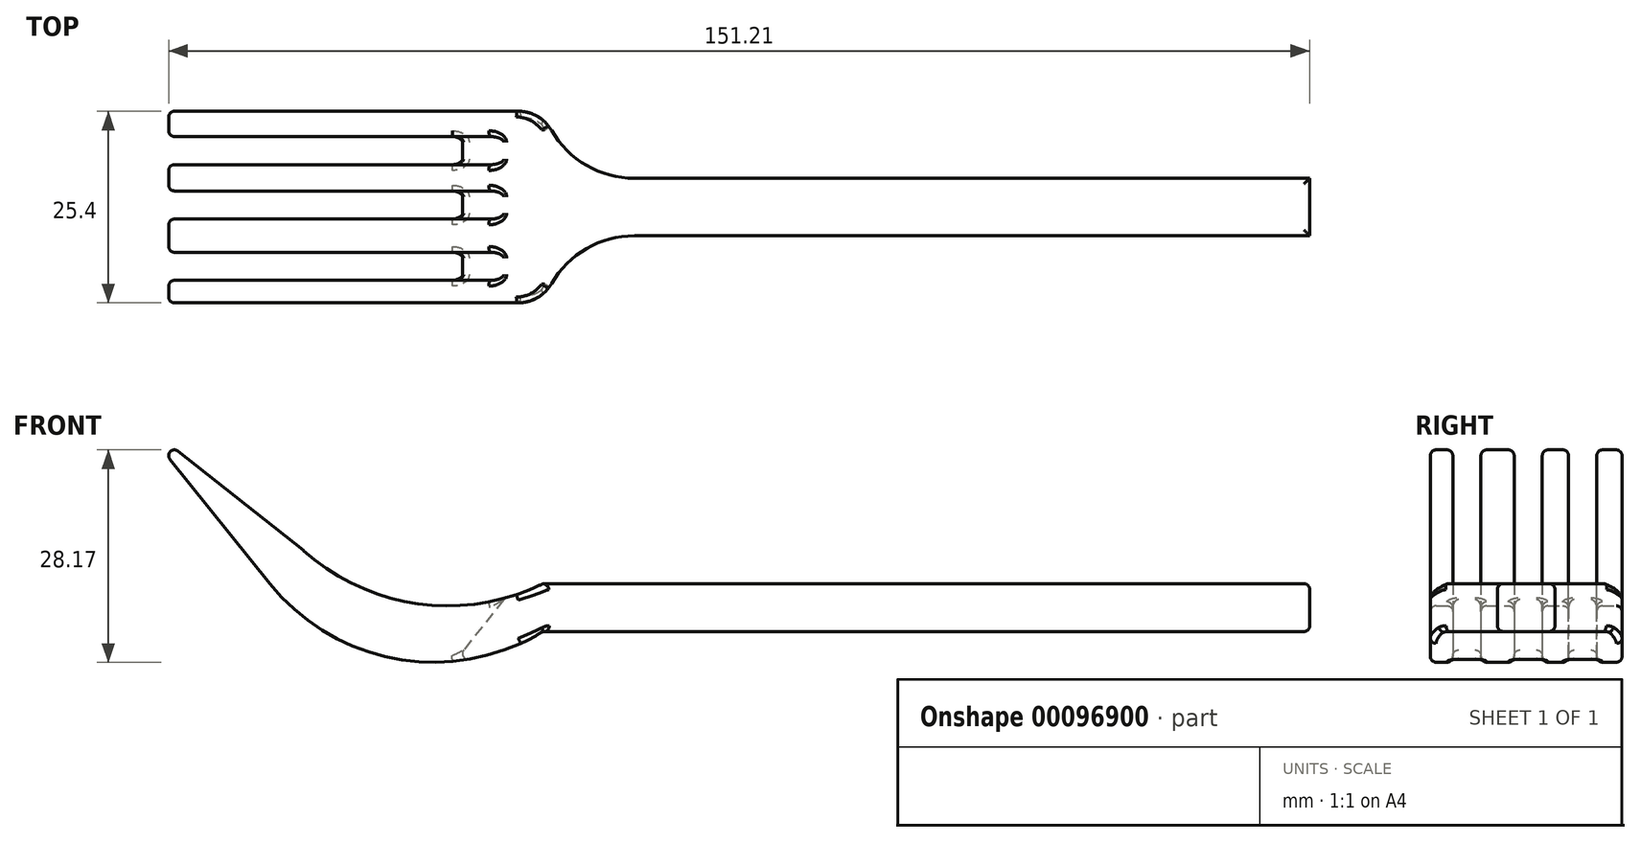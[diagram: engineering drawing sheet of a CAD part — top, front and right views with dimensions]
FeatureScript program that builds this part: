
annotation { "Feature Type Name" : "Feature", "Feature Type Description" : "" }
export const myFeature = defineFeature(function(context is Context, id is Id, definition is map)
    precondition{}
    {
        {
            var Q0;
            Q0=qCreatedBy(makeId("Front.planeOp"),FACE);
            var sketch = newSketch(context, id + "F0", { "sketchPlane" : qUnion([Q0])});
            skLineSegment(sketch, "E0.bottom", {"start": v(-0.74, 15.4) * mm, "end": v(100.86, 15.4) * mm});
            skLineSegment(sketch, "E0.top", {"start": v(-0.74, 9.04) * mm, "end": v(100.86, 9.04) * mm});
            skLineSegment(sketch, "E0.right", {"start": v(100.86, 15.4) * mm, "end": v(100.86, 9.04) * mm});
            skArc(sketch, "E1", {"start": v(-36.94, 15.4) * mm, "mid": v(-20.03, 5.4) * mm, "end": v(-0.74, 9.04) * mm});
            skArc(sketch, "E2", {"start": v(-32.49, 19.8) * mm, "mid": v(-17.29, 12.72) * mm, "end": v(-0.74, 15.4) * mm});
            skPoint(sketch, "E3.start.orphan", {"position": v(-45.23, 31.3) * mm});
            skPoint(sketch, "E4.end.orphan", {"position": v(-49.7, 31.3) * mm});
            skLineSegment(sketch, "E5", {"start": v(-36.94, 15.4) * mm, "end": v(-54.4, 37.16) * mm});
            skLineSegment(sketch, "E6", {"start": v(-54.4, 37.16) * mm, "end": v(-32.49, 19.8) * mm});
            skSolve(sketch);
        }
        {
            var Q0;
            Q0=makeQuery(id+"F0.imprint","IMPRINT",FACE,{"disambiguationData":[TD([[makeQuery(id+"F0.imprint","IMPRINT",EDGE,{"derivedFrom":sQuery(id+"F0.wireOp",EDGE,"E0.bottom")}),-1.0]])]});
            extrude(context, id + "F1", {"entities" : qUnion([Q0]), "depth" : 25.4 * mm});
        }
        {
            var Q0;
            Q0=makeQuery(id+"F1.opExtrude","SWEPT_FACE",FACE,{"disambiguationData":[OSD([sQuery(id+"F0.wireOp",EDGE,"E0.bottom")])]});
            var sketch = newSketch(context, id + "F2", { "sketchPlane" : qUnion([Q0])});
            skLineSegment(sketch, "E7.bottom", {"start": v(100.86, -25.4) * mm, "end": v(-0.74, -25.4) * mm});
            skLineSegment(sketch, "E7.top", {"start": v(100.86, -16.51) * mm, "end": v(-0.74, -16.51) * mm});
            skLineSegment(sketch, "E7.left", {"start": v(100.86, -25.4) * mm, "end": v(100.86, -16.51) * mm});
            skLineSegment(sketch, "E7.right", {"start": v(-0.74, -25.4) * mm, "end": v(-0.74, -16.51) * mm});
            skLineSegment(sketch, "E8.bottom", {"start": v(100.86, 0) * mm, "end": v(-0.74, 0) * mm});
            skLineSegment(sketch, "E8.top", {"start": v(100.86, -8.9) * mm, "end": v(-0.74, -8.9) * mm});
            skLineSegment(sketch, "E8.left", {"start": v(100.86, 0) * mm, "end": v(100.86, -8.9) * mm});
            skLineSegment(sketch, "E8.right", {"start": v(-0.74, 0) * mm, "end": v(-0.74, -8.9) * mm});
            skSolve(sketch);
        }
        {
            var Q0;
            Q0 = qSketchRegion(id + "F2", true);
            extrude(context, id + "F3", {"entities" : qUnion([Q0]), "operationType" : NewBodyOperationType.REMOVE, "oppositeDirection" : true, "depth" : 25.4 * mm});
        }
        {
            var Q0;
            Q0=makeQuery(id+"F1.opExtrude","SWEPT_FACE",FACE,{"disambiguationData":[OSD([sQuery(id+"F0.wireOp",EDGE,"E6")])]});
            var sketch = newSketch(context, id + "F4", { "sketchPlane" : qUnion([Q0])});
            skLineSegment(sketch, "E9.bottom", {"start": v(-12.9, -18.7) * mm, "end": v(-65.72, -18.7) * mm});
            skLineSegment(sketch, "E9.top", {"start": v(-12.9, -22.43) * mm, "end": v(-65.72, -22.43) * mm});
            skLineSegment(sketch, "E9.left", {"start": v(-12.9, -18.7) * mm, "end": v(-12.9, -22.43) * mm});
            skLineSegment(sketch, "E9.right", {"start": v(-65.72, -18.7) * mm, "end": v(-65.72, -22.43) * mm});
            skLineSegment(sketch, "E10.bottom", {"start": v(-65.72, -3.35) * mm, "end": v(-12.9, -3.35) * mm});
            skLineSegment(sketch, "E10.top", {"start": v(-65.72, -7.08) * mm, "end": v(-12.9, -7.08) * mm});
            skLineSegment(sketch, "E10.left", {"start": v(-65.72, -3.35) * mm, "end": v(-65.72, -7.08) * mm});
            skLineSegment(sketch, "E10.right", {"start": v(-12.9, -3.35) * mm, "end": v(-12.9, -7.08) * mm});
            skLineSegment(sketch, "E11.bottom", {"start": v(-12.9, -10.57) * mm, "end": v(-65.72, -10.57) * mm});
            skLineSegment(sketch, "E11.top", {"start": v(-12.9, -14.3) * mm, "end": v(-65.72, -14.3) * mm});
            skLineSegment(sketch, "E11.left", {"start": v(-12.9, -10.57) * mm, "end": v(-12.9, -14.3) * mm});
            skLineSegment(sketch, "E11.right", {"start": v(-65.72, -10.57) * mm, "end": v(-65.72, -14.3) * mm});
            skSolve(sketch);
        }
        {
            var Q0;
            Q0 = qSketchRegion(id + "F4", true);
            extrude(context, id + "F5", {"entities" : qUnion([Q0]), "operationType" : NewBodyOperationType.REMOVE, "endBound" : BoundingType.SYMMETRIC, "depth" : 25.4 * mm});
        }
        {
            var Q0;
            Q0=makeQuery(id+"F3.boolean.opBoolean","COPY",EDGE,{"derivedFrom":makeQuery(id+"F3.opExtrude","SWEPT_EDGE",EDGE,{"disambiguationData":[OSD([sQuery(id+"F0.wireOp",EDGE,"E0.bottom"),sQuery(id+"F0.wireOp",EDGE,"E2"),sQuery(id+"F2.wireOp",EDGE,"E8.top"),sQuery(id+"F2.wireOp",EDGE,"E8.right")])]})});
            var Q1;
            Q1=makeQuery(id+"F3.boolean.opBoolean","COPY",EDGE,{"derivedFrom":makeQuery(id+"F3.opExtrude","SWEPT_EDGE",EDGE,{"disambiguationData":[OSD([sQuery(id+"F0.wireOp",EDGE,"E0.bottom"),sQuery(id+"F0.wireOp",EDGE,"E2"),sQuery(id+"F2.wireOp",EDGE,"E7.top"),sQuery(id+"F2.wireOp",EDGE,"E7.right")])]})});
            fillet(context, id + "F6", {"entities" : qUnion([Q0, Q1]), "radius" : 12.7 * mm, "tangentPropagation" : true, "allowEdgeOverflow" : false});
        }
        {
            var Q0;
            {var subQ0=sQuery(id+"F0.wireOp",EDGE,"E2");var subQ1=sQuery(id+"F0.wireOp",EDGE,"E0.bottom");Q0=makeQuery(id+"F6.opFillet","BLEND_EDGE",EDGE,{"blendedFrom":[makeQuery(id+"F3.boolean.opBoolean","COPY",EDGE,{"derivedFrom":makeQuery(id+"F3.opExtrude","SWEPT_EDGE",EDGE,{"disambiguationData":[OSD([subQ1,subQ0,sQuery(id+"F2.wireOp",EDGE,"E7.top"),sQuery(id+"F2.wireOp",EDGE,"E7.right")])]})}),makeQuery(id+"F1.opExtrude","CAP_FACE",FACE,{"disambiguationData":[OSD([subQ1,sQuery(id+"F0.wireOp",EDGE,"E0.top"),sQuery(id+"F0.wireOp",EDGE,"E0.right"),sQuery(id+"F0.wireOp",EDGE,"E1"),subQ0,sQuery(id+"F0.wireOp",EDGE,"E5"),sQuery(id+"F0.wireOp",EDGE,"E6")])],"isStart":false})],"blendedInto":[makeQuery(id+"F1.opExtrude","CAP_FACE",FACE,{"disambiguationData":[OSD([subQ1,sQuery(id+"F0.wireOp",EDGE,"E0.top"),sQuery(id+"F0.wireOp",EDGE,"E0.right"),sQuery(id+"F0.wireOp",EDGE,"E1"),subQ0,sQuery(id+"F0.wireOp",EDGE,"E5"),sQuery(id+"F0.wireOp",EDGE,"E6")])],"isStart":false})]});}
            var Q1;
            {var subQ0=sQuery(id+"F0.wireOp",EDGE,"E2");var subQ1=sQuery(id+"F0.wireOp",EDGE,"E0.bottom");Q1=makeQuery(id+"F6.opFillet","BLEND_EDGE",EDGE,{"blendedFrom":[makeQuery(id+"F3.boolean.opBoolean","COPY",EDGE,{"derivedFrom":makeQuery(id+"F3.opExtrude","SWEPT_EDGE",EDGE,{"disambiguationData":[OSD([subQ1,subQ0,sQuery(id+"F2.wireOp",EDGE,"E8.top"),sQuery(id+"F2.wireOp",EDGE,"E8.right")])]})}),makeQuery(id+"F1.opExtrude","CAP_FACE",FACE,{"disambiguationData":[OSD([subQ1,sQuery(id+"F0.wireOp",EDGE,"E0.top"),sQuery(id+"F0.wireOp",EDGE,"E0.right"),sQuery(id+"F0.wireOp",EDGE,"E1"),subQ0,sQuery(id+"F0.wireOp",EDGE,"E5"),sQuery(id+"F0.wireOp",EDGE,"E6")])],"isStart":true})],"blendedInto":[makeQuery(id+"F1.opExtrude","CAP_FACE",FACE,{"disambiguationData":[OSD([subQ1,sQuery(id+"F0.wireOp",EDGE,"E0.top"),sQuery(id+"F0.wireOp",EDGE,"E0.right"),sQuery(id+"F0.wireOp",EDGE,"E1"),subQ0,sQuery(id+"F0.wireOp",EDGE,"E5"),sQuery(id+"F0.wireOp",EDGE,"E6")])],"isStart":true})]});}
            fillet(context, id + "F7", {"entities" : qUnion([Q0, Q1]), "radius" : 5.08 * mm, "tangentPropagation" : true, "allowEdgeOverflow" : false});
        }
        {
            var Q0;
            Q0=makeQuery(id+"F1.opExtrude","CAP_EDGE",EDGE,{"disambiguationData":[OSD([sQuery(id+"F0.wireOp",EDGE,"E2")])],"isStart":true});
            var Q1;
            Q1=makeQuery(id+"F1.opExtrude","CAP_EDGE",EDGE,{"disambiguationData":[OSD([sQuery(id+"F0.wireOp",EDGE,"E2")])],"isStart":false});
            var Q2;
            Q2=makeQuery(id+"F6.opFillet","BLEND_EDGE",EDGE,{"blendedFrom":[makeQuery(id+"F3.boolean.opBoolean","COPY",EDGE,{"derivedFrom":makeQuery(id+"F3.opExtrude","SWEPT_EDGE",EDGE,{"disambiguationData":[OSD([sQuery(id+"F0.wireOp",EDGE,"E0.bottom"),sQuery(id+"F0.wireOp",EDGE,"E2"),sQuery(id+"F2.wireOp",EDGE,"E7.top"),sQuery(id+"F2.wireOp",EDGE,"E7.right")])]})}),makeQuery(id+"F1.opExtrude","SWEPT_FACE",FACE,{"disambiguationData":[OSD([sQuery(id+"F0.wireOp",EDGE,"E0.top")])]})],"blendedInto":[makeQuery(id+"F1.opExtrude","SWEPT_FACE",FACE,{"disambiguationData":[OSD([sQuery(id+"F0.wireOp",EDGE,"E0.top")])]})]});
            var Q3;
            {var subQ0=sQuery(id+"F0.wireOp",EDGE,"E0.bottom");Q3=makeQuery(id+"F6.opFillet","BLEND_EDGE",EDGE,{"blendedFrom":[makeQuery(id+"F3.boolean.opBoolean","COPY",EDGE,{"derivedFrom":makeQuery(id+"F3.opExtrude","SWEPT_EDGE",EDGE,{"disambiguationData":[OSD([subQ0,sQuery(id+"F0.wireOp",EDGE,"E2"),sQuery(id+"F2.wireOp",EDGE,"E8.top"),sQuery(id+"F2.wireOp",EDGE,"E8.right")])]})}),makeQuery(id+"F1.opExtrude","SWEPT_FACE",FACE,{"disambiguationData":[OSD([subQ0])]})],"blendedInto":[makeQuery(id+"F1.opExtrude","SWEPT_FACE",FACE,{"disambiguationData":[OSD([subQ0])]})]});}
            var Q4;
            Q4=makeQuery(id+"F3.boolean.opBoolean","SPLIT",EDGE,{"derivedFrom":makeQuery(id+"F1.opExtrude","SWEPT_EDGE",EDGE,{"disambiguationData":[OSD([sQuery(id+"F0.wireOp",EDGE,"E0.bottom"),sQuery(id+"F0.wireOp",EDGE,"E2")])]})});
            var Q5;
            Q5=makeQuery(id+"F1.opExtrude","CAP_EDGE",EDGE,{"disambiguationData":[OSD([sQuery(id+"F0.wireOp",EDGE,"E1")])],"isStart":false});
            var Q6;
            {var subQ0=sQuery(id+"F0.wireOp",EDGE,"E2");var subQ1=sQuery(id+"F0.wireOp",EDGE,"E0.bottom");Q6=makeQuery(id+"F7.opFillet","BLEND_EDGE",EDGE,{"blendedFrom":[makeQuery(id+"F6.opFillet","BLEND_EDGE",EDGE,{"blendedFrom":[makeQuery(id+"F3.boolean.opBoolean","COPY",EDGE,{"derivedFrom":makeQuery(id+"F3.opExtrude","SWEPT_EDGE",EDGE,{"disambiguationData":[OSD([subQ1,subQ0,sQuery(id+"F2.wireOp",EDGE,"E8.top"),sQuery(id+"F2.wireOp",EDGE,"E8.right")])]})}),makeQuery(id+"F1.opExtrude","CAP_FACE",FACE,{"disambiguationData":[OSD([subQ1,sQuery(id+"F0.wireOp",EDGE,"E0.top"),sQuery(id+"F0.wireOp",EDGE,"E0.right"),sQuery(id+"F0.wireOp",EDGE,"E1"),subQ0,sQuery(id+"F0.wireOp",EDGE,"E5"),sQuery(id+"F0.wireOp",EDGE,"E6")])],"isStart":true})],"blendedInto":[makeQuery(id+"F1.opExtrude","CAP_FACE",FACE,{"disambiguationData":[OSD([subQ1,sQuery(id+"F0.wireOp",EDGE,"E0.top"),sQuery(id+"F0.wireOp",EDGE,"E0.right"),sQuery(id+"F0.wireOp",EDGE,"E1"),subQ0,sQuery(id+"F0.wireOp",EDGE,"E5"),sQuery(id+"F0.wireOp",EDGE,"E6")])],"isStart":true})]}),makeQuery(id+"F1.opExtrude","SWEPT_FACE",FACE,{"disambiguationData":[OSD([subQ0])]})],"blendedInto":[makeQuery(id+"F1.opExtrude","SWEPT_FACE",FACE,{"disambiguationData":[OSD([subQ0])]})]});}
            var Q7;
            Q7=makeQuery(id+"F1.opExtrude","CAP_EDGE",EDGE,{"disambiguationData":[OSD([sQuery(id+"F0.wireOp",EDGE,"E6")])],"isStart":true});
            var Q8;
            Q8=makeQuery(id+"F5.boolean.opBoolean","INTERSECT",EDGE,{"derivedFrom":[makeQuery(id+"F1.opExtrude","SWEPT_FACE",FACE,{"disambiguationData":[OSD([sQuery(id+"F0.wireOp",EDGE,"E2")])]}),makeQuery(id+"F5.opExtrude","SWEPT_FACE",FACE,{"disambiguationData":[OSD([sQuery(id+"F4.wireOp",EDGE,"E9.top")])]})]});
            var Q9;
            {var subQ0=sQuery(id+"F2.wireOp",EDGE,"E7.top");Q9=makeQuery(id+"F6.opFillet","BLEND_EDGE",EDGE,{"blendedFrom":[makeQuery(id+"F3.boolean.opBoolean","COPY",EDGE,{"derivedFrom":makeQuery(id+"F3.opExtrude","SWEPT_EDGE",EDGE,{"disambiguationData":[OSD([sQuery(id+"F0.wireOp",EDGE,"E0.bottom"),sQuery(id+"F0.wireOp",EDGE,"E2"),subQ0,sQuery(id+"F2.wireOp",EDGE,"E7.right")])]})}),makeQuery(id+"F3.boolean.opBoolean","COPY",FACE,{"derivedFrom":makeQuery(id+"F3.opExtrude","SWEPT_FACE",FACE,{"disambiguationData":[OSD([subQ0])]})})],"blendedInto":[makeQuery(id+"F3.boolean.opBoolean","COPY",FACE,{"derivedFrom":makeQuery(id+"F3.opExtrude","SWEPT_FACE",FACE,{"disambiguationData":[OSD([subQ0])]})})]});}
            var Q10;
            Q10=makeQuery(id+"F5.boolean.opBoolean","INTERSECT",EDGE,{"derivedFrom":[makeQuery(id+"F1.opExtrude","SWEPT_FACE",FACE,{"disambiguationData":[OSD([sQuery(id+"F0.wireOp",EDGE,"E2")])]}),makeQuery(id+"F5.opExtrude","SWEPT_FACE",FACE,{"disambiguationData":[OSD([sQuery(id+"F4.wireOp",EDGE,"E9.bottom")])]})]});
            var Q11;
            Q11=makeQuery(id+"F5.boolean.opBoolean","INTERSECT",EDGE,{"derivedFrom":[makeQuery(id+"F1.opExtrude","SWEPT_FACE",FACE,{"disambiguationData":[OSD([sQuery(id+"F0.wireOp",EDGE,"E2")])]}),makeQuery(id+"F5.opExtrude","SWEPT_FACE",FACE,{"disambiguationData":[OSD([sQuery(id+"F4.wireOp",EDGE,"E10.top")])]})]});
            var Q12;
            Q12=makeQuery(id+"F5.boolean.opBoolean","INTERSECT",EDGE,{"derivedFrom":[makeQuery(id+"F1.opExtrude","SWEPT_FACE",FACE,{"disambiguationData":[OSD([sQuery(id+"F0.wireOp",EDGE,"E2")])]}),makeQuery(id+"F5.opExtrude","SWEPT_FACE",FACE,{"disambiguationData":[OSD([sQuery(id+"F4.wireOp",EDGE,"E10.bottom")])]})]});
            var Q13;
            Q13=makeQuery(id+"F1.opExtrude","CAP_EDGE",EDGE,{"disambiguationData":[OSD([sQuery(id+"F0.wireOp",EDGE,"E5")])],"isStart":false});
            var Q14;
            Q14=makeQuery(id+"F3.boolean.opBoolean","COPY",EDGE,{"derivedFrom":makeQuery(id+"F3.opExtrude","CAP_EDGE",EDGE,{"disambiguationData":[OSD([sQuery(id+"F2.wireOp",EDGE,"E7.top")])],"isStart":true})});
            var Q15;
            Q15=makeQuery(id+"F3.boolean.opBoolean","COPY",EDGE,{"derivedFrom":makeQuery(id+"F3.opExtrude","CAP_EDGE",EDGE,{"disambiguationData":[OSD([sQuery(id+"F2.wireOp",EDGE,"E8.top")])],"isStart":true})});
            var Q16;
            Q16=makeQuery(id+"F3.boolean.opBoolean","INTERSECT",EDGE,{"derivedFrom":[makeQuery(id+"F1.opExtrude","SWEPT_FACE",FACE,{"disambiguationData":[OSD([sQuery(id+"F0.wireOp",EDGE,"E0.top")])]}),makeQuery(id+"F3.opExtrude","SWEPT_FACE",FACE,{"disambiguationData":[OSD([sQuery(id+"F2.wireOp",EDGE,"E7.top")])]})]});
            var Q17;
            Q17=makeQuery(id+"F3.boolean.opBoolean","COPY",EDGE,{"derivedFrom":makeQuery(id+"F3.opExtrude","SWEPT_EDGE",EDGE,{"disambiguationData":[OSD([sQuery(id+"F0.wireOp",EDGE,"E0.bottom"),sQuery(id+"F0.wireOp",EDGE,"E0.right"),sQuery(id+"F2.wireOp",EDGE,"E8.top"),sQuery(id+"F2.wireOp",EDGE,"E8.left")])]})});
            var Q18;
            {var subQ0=sQuery(id+"F0.wireOp",EDGE,"E2");var subQ1=sQuery(id+"F0.wireOp",EDGE,"E0.bottom");Q18=makeQuery(id+"F7.opFillet","BLEND_EDGE",EDGE,{"blendedFrom":[makeQuery(id+"F6.opFillet","BLEND_EDGE",EDGE,{"blendedFrom":[makeQuery(id+"F3.boolean.opBoolean","COPY",EDGE,{"derivedFrom":makeQuery(id+"F3.opExtrude","SWEPT_EDGE",EDGE,{"disambiguationData":[OSD([subQ1,subQ0,sQuery(id+"F2.wireOp",EDGE,"E7.top"),sQuery(id+"F2.wireOp",EDGE,"E7.right")])]})}),makeQuery(id+"F1.opExtrude","CAP_FACE",FACE,{"disambiguationData":[OSD([subQ1,sQuery(id+"F0.wireOp",EDGE,"E0.top"),sQuery(id+"F0.wireOp",EDGE,"E0.right"),sQuery(id+"F0.wireOp",EDGE,"E1"),subQ0,sQuery(id+"F0.wireOp",EDGE,"E5"),sQuery(id+"F0.wireOp",EDGE,"E6")])],"isStart":false})],"blendedInto":[makeQuery(id+"F1.opExtrude","CAP_FACE",FACE,{"disambiguationData":[OSD([subQ1,sQuery(id+"F0.wireOp",EDGE,"E0.top"),sQuery(id+"F0.wireOp",EDGE,"E0.right"),sQuery(id+"F0.wireOp",EDGE,"E1"),subQ0,sQuery(id+"F0.wireOp",EDGE,"E5"),sQuery(id+"F0.wireOp",EDGE,"E6")])],"isStart":false})]}),makeQuery(id+"F1.opExtrude","SWEPT_FACE",FACE,{"disambiguationData":[OSD([subQ0])]})],"blendedInto":[makeQuery(id+"F1.opExtrude","SWEPT_FACE",FACE,{"disambiguationData":[OSD([subQ0])]})]});}
            var Q19;
            Q19=makeQuery(id+"F3.boolean.opBoolean","COPY",EDGE,{"derivedFrom":makeQuery(id+"F3.opExtrude","SWEPT_EDGE",EDGE,{"disambiguationData":[OSD([sQuery(id+"F0.wireOp",EDGE,"E0.bottom"),sQuery(id+"F0.wireOp",EDGE,"E0.right"),sQuery(id+"F2.wireOp",EDGE,"E7.top"),sQuery(id+"F2.wireOp",EDGE,"E7.left")])]})});
            var Q20;
            {var subQ0=sQuery(id+"F0.wireOp",EDGE,"E1");var subQ1=sQuery(id+"F0.wireOp",EDGE,"E2");var subQ2=sQuery(id+"F0.wireOp",EDGE,"E0.bottom");Q20=makeQuery(id+"F7.opFillet","BLEND_EDGE",EDGE,{"blendedFrom":[makeQuery(id+"F6.opFillet","BLEND_EDGE",EDGE,{"blendedFrom":[makeQuery(id+"F3.boolean.opBoolean","COPY",EDGE,{"derivedFrom":makeQuery(id+"F3.opExtrude","SWEPT_EDGE",EDGE,{"disambiguationData":[OSD([subQ2,subQ1,sQuery(id+"F2.wireOp",EDGE,"E7.top"),sQuery(id+"F2.wireOp",EDGE,"E7.right")])]})}),makeQuery(id+"F1.opExtrude","CAP_FACE",FACE,{"disambiguationData":[OSD([subQ2,sQuery(id+"F0.wireOp",EDGE,"E0.top"),sQuery(id+"F0.wireOp",EDGE,"E0.right"),subQ0,subQ1,sQuery(id+"F0.wireOp",EDGE,"E5"),sQuery(id+"F0.wireOp",EDGE,"E6")])],"isStart":false})],"blendedInto":[makeQuery(id+"F1.opExtrude","CAP_FACE",FACE,{"disambiguationData":[OSD([subQ2,sQuery(id+"F0.wireOp",EDGE,"E0.top"),sQuery(id+"F0.wireOp",EDGE,"E0.right"),subQ0,subQ1,sQuery(id+"F0.wireOp",EDGE,"E5"),sQuery(id+"F0.wireOp",EDGE,"E6")])],"isStart":false})]}),makeQuery(id+"F1.opExtrude","SWEPT_FACE",FACE,{"disambiguationData":[OSD([subQ0])]})],"blendedInto":[makeQuery(id+"F1.opExtrude","SWEPT_FACE",FACE,{"disambiguationData":[OSD([subQ0])]})]});}
            var Q21;
            {var subQ0=sQuery(id+"F0.wireOp",EDGE,"E0.bottom");Q21=makeQuery(id+"F6.opFillet","BLEND_EDGE",EDGE,{"blendedFrom":[makeQuery(id+"F3.boolean.opBoolean","COPY",EDGE,{"derivedFrom":makeQuery(id+"F3.opExtrude","SWEPT_EDGE",EDGE,{"disambiguationData":[OSD([subQ0,sQuery(id+"F0.wireOp",EDGE,"E2"),sQuery(id+"F2.wireOp",EDGE,"E7.top"),sQuery(id+"F2.wireOp",EDGE,"E7.right")])]})}),makeQuery(id+"F1.opExtrude","SWEPT_FACE",FACE,{"disambiguationData":[OSD([subQ0])]})],"blendedInto":[makeQuery(id+"F1.opExtrude","SWEPT_FACE",FACE,{"disambiguationData":[OSD([subQ0])]})]});}
            var Q22;
            Q22=makeQuery(id+"F5.boolean.opBoolean","INTERSECT",EDGE,{"derivedFrom":[makeQuery(id+"F1.opExtrude","SWEPT_FACE",FACE,{"disambiguationData":[OSD([sQuery(id+"F0.wireOp",EDGE,"E2")])]}),makeQuery(id+"F5.opExtrude","SWEPT_FACE",FACE,{"disambiguationData":[OSD([sQuery(id+"F4.wireOp",EDGE,"E11.top")])]})]});
            var Q23;
            Q23=makeQuery(id+"F5.boolean.opBoolean","INTERSECT",EDGE,{"derivedFrom":[makeQuery(id+"F1.opExtrude","SWEPT_FACE",FACE,{"disambiguationData":[OSD([sQuery(id+"F0.wireOp",EDGE,"E6")])]}),makeQuery(id+"F5.opExtrude","SWEPT_FACE",FACE,{"disambiguationData":[OSD([sQuery(id+"F4.wireOp",EDGE,"E10.top")])]})]});
            var Q24;
            Q24=makeQuery(id+"F5.boolean.opBoolean","INTERSECT",EDGE,{"derivedFrom":[makeQuery(id+"F1.opExtrude","SWEPT_FACE",FACE,{"disambiguationData":[OSD([sQuery(id+"F0.wireOp",EDGE,"E2")])]}),makeQuery(id+"F5.opExtrude","SWEPT_FACE",FACE,{"disambiguationData":[OSD([sQuery(id+"F4.wireOp",EDGE,"E11.bottom")])]})]});
            var Q25;
            Q25=makeQuery(id+"F5.boolean.opBoolean","INTERSECT",EDGE,{"derivedFrom":[makeQuery(id+"F1.opExtrude","SWEPT_FACE",FACE,{"disambiguationData":[OSD([sQuery(id+"F0.wireOp",EDGE,"E6")])]}),makeQuery(id+"F5.opExtrude","SWEPT_FACE",FACE,{"disambiguationData":[OSD([sQuery(id+"F4.wireOp",EDGE,"E10.bottom")])]})]});
            var Q26;
            Q26=makeQuery(id+"F5.boolean.opBoolean","INTERSECT",EDGE,{"derivedFrom":[makeQuery(id+"F1.opExtrude","SWEPT_FACE",FACE,{"disambiguationData":[OSD([sQuery(id+"F0.wireOp",EDGE,"E6")])]}),makeQuery(id+"F5.opExtrude","SWEPT_FACE",FACE,{"disambiguationData":[OSD([sQuery(id+"F4.wireOp",EDGE,"E9.top")])]})]});
            var Q27;
            Q27=makeQuery(id+"F5.boolean.opBoolean","INTERSECT",EDGE,{"derivedFrom":[makeQuery(id+"F1.opExtrude","SWEPT_FACE",FACE,{"disambiguationData":[OSD([sQuery(id+"F0.wireOp",EDGE,"E6")])]}),makeQuery(id+"F5.opExtrude","SWEPT_FACE",FACE,{"disambiguationData":[OSD([sQuery(id+"F4.wireOp",EDGE,"E9.bottom")])]})]});
            var Q28;
            Q28=makeQuery(id+"F5.boolean.opBoolean","INTERSECT",EDGE,{"derivedFrom":[makeQuery(id+"F1.opExtrude","SWEPT_FACE",FACE,{"disambiguationData":[OSD([sQuery(id+"F0.wireOp",EDGE,"E5")])]}),makeQuery(id+"F5.opExtrude","SWEPT_FACE",FACE,{"disambiguationData":[OSD([sQuery(id+"F4.wireOp",EDGE,"E9.bottom")])]})]});
            var Q29;
            Q29=makeQuery(id+"F5.boolean.opBoolean","INTERSECT",EDGE,{"derivedFrom":[makeQuery(id+"F1.opExtrude","SWEPT_FACE",FACE,{"disambiguationData":[OSD([sQuery(id+"F0.wireOp",EDGE,"E6")])]}),makeQuery(id+"F5.opExtrude","SWEPT_FACE",FACE,{"disambiguationData":[OSD([sQuery(id+"F4.wireOp",EDGE,"E11.top")])]})]});
            var Q30;
            Q30=makeQuery(id+"F5.boolean.opBoolean","INTERSECT",EDGE,{"derivedFrom":[makeQuery(id+"F1.opExtrude","SWEPT_FACE",FACE,{"disambiguationData":[OSD([sQuery(id+"F0.wireOp",EDGE,"E6")])]}),makeQuery(id+"F5.opExtrude","SWEPT_FACE",FACE,{"disambiguationData":[OSD([sQuery(id+"F4.wireOp",EDGE,"E11.bottom")])]})]});
            var Q31;
            Q31=makeQuery(id+"F1.opExtrude","CAP_EDGE",EDGE,{"disambiguationData":[OSD([sQuery(id+"F0.wireOp",EDGE,"E6")])],"isStart":false});
            var Q32;
            {var subQ0=sQuery(id+"F0.wireOp",EDGE,"E2");var subQ1=sQuery(id+"F0.wireOp",EDGE,"E0.bottom");var subQ2=makeQuery(id+"F1.opExtrude","CAP_FACE",FACE,{"disambiguationData":[OSD([subQ1,sQuery(id+"F0.wireOp",EDGE,"E0.top"),sQuery(id+"F0.wireOp",EDGE,"E0.right"),sQuery(id+"F0.wireOp",EDGE,"E1"),subQ0,sQuery(id+"F0.wireOp",EDGE,"E5"),sQuery(id+"F0.wireOp",EDGE,"E6")])],"isStart":false});Q32=makeQuery(id+"F7.opFillet","BLEND_EDGE",EDGE,{"blendedFrom":[makeQuery(id+"F6.opFillet","BLEND_EDGE",EDGE,{"blendedFrom":[makeQuery(id+"F3.boolean.opBoolean","COPY",EDGE,{"derivedFrom":makeQuery(id+"F3.opExtrude","SWEPT_EDGE",EDGE,{"disambiguationData":[OSD([subQ1,subQ0,sQuery(id+"F2.wireOp",EDGE,"E7.top"),sQuery(id+"F2.wireOp",EDGE,"E7.right")])]})}),subQ2],"blendedInto":[subQ2]}),subQ2],"blendedInto":[subQ2]});}
            var Q33;
            {var subQ0=sQuery(id+"F0.wireOp",EDGE,"E2");var subQ1=sQuery(id+"F0.wireOp",EDGE,"E0.bottom");var subQ2=makeQuery(id+"F1.opExtrude","CAP_FACE",FACE,{"disambiguationData":[OSD([subQ1,sQuery(id+"F0.wireOp",EDGE,"E0.top"),sQuery(id+"F0.wireOp",EDGE,"E0.right"),sQuery(id+"F0.wireOp",EDGE,"E1"),subQ0,sQuery(id+"F0.wireOp",EDGE,"E5"),sQuery(id+"F0.wireOp",EDGE,"E6")])],"isStart":true});Q33=makeQuery(id+"F7.opFillet","BLEND_EDGE",EDGE,{"blendedFrom":[makeQuery(id+"F6.opFillet","BLEND_EDGE",EDGE,{"blendedFrom":[makeQuery(id+"F3.boolean.opBoolean","COPY",EDGE,{"derivedFrom":makeQuery(id+"F3.opExtrude","SWEPT_EDGE",EDGE,{"disambiguationData":[OSD([subQ1,subQ0,sQuery(id+"F2.wireOp",EDGE,"E8.top"),sQuery(id+"F2.wireOp",EDGE,"E8.right")])]})}),subQ2],"blendedInto":[subQ2]}),subQ2],"blendedInto":[subQ2]});}
            var Q34;
            {var subQ0=sQuery(id+"F0.wireOp",EDGE,"E1");var subQ1=sQuery(id+"F0.wireOp",EDGE,"E0.top");Q34=makeQuery(id+"F3.boolean.opBoolean","SPLIT",EDGE,{"disambiguationData":[TD([makeQuery(id+"F1.opExtrude","SWEPT_FACE",FACE,{"disambiguationData":[OSD([subQ1])]}),makeQuery(id+"F1.opExtrude","SWEPT_FACE",FACE,{"disambiguationData":[OSD([subQ0])]}),makeQuery(id+"F3.opExtrude","SWEPT_FACE",FACE,{"disambiguationData":[OSD([sQuery(id+"F2.wireOp",EDGE,"E7.top")])]}),makeQuery(id+"F3.opExtrude","SWEPT_FACE",FACE,{"disambiguationData":[OSD([sQuery(id+"F2.wireOp",EDGE,"E7.right")])]}),makeQuery(id+"F3.opExtrude","SWEPT_FACE",FACE,{"disambiguationData":[OSD([sQuery(id+"F2.wireOp",EDGE,"E8.top")])]}),makeQuery(id+"F3.opExtrude","SWEPT_FACE",FACE,{"disambiguationData":[OSD([sQuery(id+"F2.wireOp",EDGE,"E8.right")])]})])],"derivedFrom":makeQuery(id+"F1.opExtrude","SWEPT_EDGE",EDGE,{"disambiguationData":[OSD([subQ1,subQ0])]})});}
            var Q35;
            Q35=makeQuery(id+"F6.opFillet","BLEND_EDGE",EDGE,{"blendedFrom":[makeQuery(id+"F3.boolean.opBoolean","COPY",EDGE,{"derivedFrom":makeQuery(id+"F3.opExtrude","SWEPT_EDGE",EDGE,{"disambiguationData":[OSD([sQuery(id+"F0.wireOp",EDGE,"E0.bottom"),sQuery(id+"F0.wireOp",EDGE,"E2"),sQuery(id+"F2.wireOp",EDGE,"E8.top"),sQuery(id+"F2.wireOp",EDGE,"E8.right")])]})}),makeQuery(id+"F1.opExtrude","SWEPT_FACE",FACE,{"disambiguationData":[OSD([sQuery(id+"F0.wireOp",EDGE,"E0.top")])]})],"blendedInto":[makeQuery(id+"F1.opExtrude","SWEPT_FACE",FACE,{"disambiguationData":[OSD([sQuery(id+"F0.wireOp",EDGE,"E0.top")])]})]});
            var Q36;
            Q36=makeQuery(id+"F1.opExtrude","CAP_EDGE",EDGE,{"disambiguationData":[OSD([sQuery(id+"F0.wireOp",EDGE,"E1")])],"isStart":true});
            var Q37;
            {var subQ0=sQuery(id+"F0.wireOp",EDGE,"E1");var subQ1=sQuery(id+"F0.wireOp",EDGE,"E2");var subQ2=sQuery(id+"F0.wireOp",EDGE,"E0.bottom");Q37=makeQuery(id+"F7.opFillet","BLEND_EDGE",EDGE,{"blendedFrom":[makeQuery(id+"F6.opFillet","BLEND_EDGE",EDGE,{"blendedFrom":[makeQuery(id+"F3.boolean.opBoolean","COPY",EDGE,{"derivedFrom":makeQuery(id+"F3.opExtrude","SWEPT_EDGE",EDGE,{"disambiguationData":[OSD([subQ2,subQ1,sQuery(id+"F2.wireOp",EDGE,"E8.top"),sQuery(id+"F2.wireOp",EDGE,"E8.right")])]})}),makeQuery(id+"F1.opExtrude","CAP_FACE",FACE,{"disambiguationData":[OSD([subQ2,sQuery(id+"F0.wireOp",EDGE,"E0.top"),sQuery(id+"F0.wireOp",EDGE,"E0.right"),subQ0,subQ1,sQuery(id+"F0.wireOp",EDGE,"E5"),sQuery(id+"F0.wireOp",EDGE,"E6")])],"isStart":true})],"blendedInto":[makeQuery(id+"F1.opExtrude","CAP_FACE",FACE,{"disambiguationData":[OSD([subQ2,sQuery(id+"F0.wireOp",EDGE,"E0.top"),sQuery(id+"F0.wireOp",EDGE,"E0.right"),subQ0,subQ1,sQuery(id+"F0.wireOp",EDGE,"E5"),sQuery(id+"F0.wireOp",EDGE,"E6")])],"isStart":true})]}),makeQuery(id+"F1.opExtrude","SWEPT_FACE",FACE,{"disambiguationData":[OSD([subQ0])]})],"blendedInto":[makeQuery(id+"F1.opExtrude","SWEPT_FACE",FACE,{"disambiguationData":[OSD([subQ0])]})]});}
            var Q38;
            Q38=makeQuery(id+"F5.boolean.opBoolean","INTERSECT",EDGE,{"derivedFrom":[makeQuery(id+"F1.opExtrude","SWEPT_FACE",FACE,{"disambiguationData":[OSD([sQuery(id+"F0.wireOp",EDGE,"E1")])]}),makeQuery(id+"F5.opExtrude","SWEPT_FACE",FACE,{"disambiguationData":[OSD([sQuery(id+"F4.wireOp",EDGE,"E10.bottom")])]})]});
            var Q39;
            Q39=makeQuery(id+"F5.boolean.opBoolean","INTERSECT",EDGE,{"derivedFrom":[makeQuery(id+"F1.opExtrude","SWEPT_FACE",FACE,{"disambiguationData":[OSD([sQuery(id+"F0.wireOp",EDGE,"E1")])]}),makeQuery(id+"F5.opExtrude","SWEPT_FACE",FACE,{"disambiguationData":[OSD([sQuery(id+"F4.wireOp",EDGE,"E9.top")])]})]});
            var Q40;
            Q40=makeQuery(id+"F5.boolean.opBoolean","INTERSECT",EDGE,{"derivedFrom":[makeQuery(id+"F1.opExtrude","SWEPT_FACE",FACE,{"disambiguationData":[OSD([sQuery(id+"F0.wireOp",EDGE,"E1")])]}),makeQuery(id+"F5.opExtrude","SWEPT_FACE",FACE,{"disambiguationData":[OSD([sQuery(id+"F4.wireOp",EDGE,"E9.bottom")])]})]});
            var Q41;
            Q41=makeQuery(id+"F5.boolean.opBoolean","COPY",EDGE,{"derivedFrom":makeQuery(id+"F5.opExtrude","SWEPT_EDGE",EDGE,{"disambiguationData":[OSD([sQuery(id+"F4.wireOp",EDGE,"E11.top"),sQuery(id+"F4.wireOp",EDGE,"E11.left")])]})});
            var Q42;
            Q42=makeQuery(id+"F5.boolean.opBoolean","COPY",EDGE,{"derivedFrom":makeQuery(id+"F5.opExtrude","SWEPT_EDGE",EDGE,{"disambiguationData":[OSD([sQuery(id+"F4.wireOp",EDGE,"E10.top"),sQuery(id+"F4.wireOp",EDGE,"E10.right")])]})});
            var Q43;
            Q43=makeQuery(id+"F5.boolean.opBoolean","COPY",EDGE,{"derivedFrom":makeQuery(id+"F5.opExtrude","SWEPT_EDGE",EDGE,{"disambiguationData":[OSD([sQuery(id+"F4.wireOp",EDGE,"E9.top"),sQuery(id+"F4.wireOp",EDGE,"E9.left")])]})});
            var Q44;
            Q44=makeQuery(id+"F5.boolean.opBoolean","COPY",EDGE,{"derivedFrom":makeQuery(id+"F5.opExtrude","SWEPT_EDGE",EDGE,{"disambiguationData":[OSD([sQuery(id+"F4.wireOp",EDGE,"E9.bottom"),sQuery(id+"F4.wireOp",EDGE,"E9.left")])]})});
            var Q45;
            Q45=makeQuery(id+"F5.boolean.opBoolean","INTERSECT",EDGE,{"derivedFrom":[makeQuery(id+"F1.opExtrude","SWEPT_FACE",FACE,{"disambiguationData":[OSD([sQuery(id+"F0.wireOp",EDGE,"E1")])]}),makeQuery(id+"F5.opExtrude","SWEPT_FACE",FACE,{"disambiguationData":[OSD([sQuery(id+"F4.wireOp",EDGE,"E10.top")])]})]});
            var Q46;
            Q46=makeQuery(id+"F1.opExtrude","SWEPT_EDGE",EDGE,{"disambiguationData":[OSD([sQuery(id+"F0.wireOp",EDGE,"E0.top"),sQuery(id+"F0.wireOp",EDGE,"E0.right")])]});
            var Q47;
            Q47=makeQuery(id+"F1.opExtrude","SWEPT_EDGE",EDGE,{"disambiguationData":[OSD([sQuery(id+"F0.wireOp",EDGE,"E0.bottom"),sQuery(id+"F0.wireOp",EDGE,"E0.right")])]});
            var Q48;
            Q48=makeQuery(id+"F5.boolean.opBoolean","INTERSECT",EDGE,{"derivedFrom":[makeQuery(id+"F1.opExtrude","SWEPT_FACE",FACE,{"disambiguationData":[OSD([sQuery(id+"F0.wireOp",EDGE,"E5")])]}),makeQuery(id+"F5.opExtrude","SWEPT_FACE",FACE,{"disambiguationData":[OSD([sQuery(id+"F4.wireOp",EDGE,"E11.bottom")])]})]});
            var Q49;
            Q49=makeQuery(id+"F3.boolean.opBoolean","INTERSECT",EDGE,{"derivedFrom":[makeQuery(id+"F1.opExtrude","SWEPT_FACE",FACE,{"disambiguationData":[OSD([sQuery(id+"F0.wireOp",EDGE,"E0.top")])]}),makeQuery(id+"F3.opExtrude","SWEPT_FACE",FACE,{"disambiguationData":[OSD([sQuery(id+"F2.wireOp",EDGE,"E8.top")])]})]});
            var Q50;
            {var subQ0=sQuery(id+"F0.wireOp",EDGE,"E0.top");var subQ1=sQuery(id+"F0.wireOp",EDGE,"E2");var subQ2=sQuery(id+"F0.wireOp",EDGE,"E0.bottom");Q50=makeQuery(id+"F7.opFillet","BLEND_EDGE",EDGE,{"blendedFrom":[makeQuery(id+"F6.opFillet","BLEND_EDGE",EDGE,{"blendedFrom":[makeQuery(id+"F3.boolean.opBoolean","COPY",EDGE,{"derivedFrom":makeQuery(id+"F3.opExtrude","SWEPT_EDGE",EDGE,{"disambiguationData":[OSD([subQ2,subQ1,sQuery(id+"F2.wireOp",EDGE,"E7.top"),sQuery(id+"F2.wireOp",EDGE,"E7.right")])]})}),makeQuery(id+"F1.opExtrude","CAP_FACE",FACE,{"disambiguationData":[OSD([subQ2,subQ0,sQuery(id+"F0.wireOp",EDGE,"E0.right"),sQuery(id+"F0.wireOp",EDGE,"E1"),subQ1,sQuery(id+"F0.wireOp",EDGE,"E5"),sQuery(id+"F0.wireOp",EDGE,"E6")])],"isStart":false})],"blendedInto":[makeQuery(id+"F1.opExtrude","CAP_FACE",FACE,{"disambiguationData":[OSD([subQ2,subQ0,sQuery(id+"F0.wireOp",EDGE,"E0.right"),sQuery(id+"F0.wireOp",EDGE,"E1"),subQ1,sQuery(id+"F0.wireOp",EDGE,"E5"),sQuery(id+"F0.wireOp",EDGE,"E6")])],"isStart":false})]}),makeQuery(id+"F1.opExtrude","SWEPT_FACE",FACE,{"disambiguationData":[OSD([subQ0])]})],"blendedInto":[makeQuery(id+"F1.opExtrude","SWEPT_FACE",FACE,{"disambiguationData":[OSD([subQ0])]})]});}
            var Q51;
            {var subQ0=sQuery(id+"F2.wireOp",EDGE,"E8.top");Q51=makeQuery(id+"F6.opFillet","BLEND_EDGE",EDGE,{"blendedFrom":[makeQuery(id+"F3.boolean.opBoolean","COPY",EDGE,{"derivedFrom":makeQuery(id+"F3.opExtrude","SWEPT_EDGE",EDGE,{"disambiguationData":[OSD([sQuery(id+"F0.wireOp",EDGE,"E0.bottom"),sQuery(id+"F0.wireOp",EDGE,"E2"),subQ0,sQuery(id+"F2.wireOp",EDGE,"E8.right")])]})}),makeQuery(id+"F3.boolean.opBoolean","COPY",FACE,{"derivedFrom":makeQuery(id+"F3.opExtrude","SWEPT_FACE",FACE,{"disambiguationData":[OSD([subQ0])]})})],"blendedInto":[makeQuery(id+"F3.boolean.opBoolean","COPY",FACE,{"derivedFrom":makeQuery(id+"F3.opExtrude","SWEPT_FACE",FACE,{"disambiguationData":[OSD([subQ0])]})})]});}
            var Q52;
            {var subQ0=sQuery(id+"F0.wireOp",EDGE,"E0.bottom");var subQ1=sQuery(id+"F0.wireOp",EDGE,"E2");Q52=makeQuery(id+"F7.opFillet","BLEND_EDGE",EDGE,{"blendedFrom":[makeQuery(id+"F6.opFillet","BLEND_EDGE",EDGE,{"blendedFrom":[makeQuery(id+"F3.boolean.opBoolean","COPY",EDGE,{"derivedFrom":makeQuery(id+"F3.opExtrude","SWEPT_EDGE",EDGE,{"disambiguationData":[OSD([subQ0,subQ1,sQuery(id+"F2.wireOp",EDGE,"E7.top"),sQuery(id+"F2.wireOp",EDGE,"E7.right")])]})}),makeQuery(id+"F1.opExtrude","CAP_FACE",FACE,{"disambiguationData":[OSD([subQ0,sQuery(id+"F0.wireOp",EDGE,"E0.top"),sQuery(id+"F0.wireOp",EDGE,"E0.right"),sQuery(id+"F0.wireOp",EDGE,"E1"),subQ1,sQuery(id+"F0.wireOp",EDGE,"E5"),sQuery(id+"F0.wireOp",EDGE,"E6")])],"isStart":false})],"blendedInto":[makeQuery(id+"F1.opExtrude","CAP_FACE",FACE,{"disambiguationData":[OSD([subQ0,sQuery(id+"F0.wireOp",EDGE,"E0.top"),sQuery(id+"F0.wireOp",EDGE,"E0.right"),sQuery(id+"F0.wireOp",EDGE,"E1"),subQ1,sQuery(id+"F0.wireOp",EDGE,"E5"),sQuery(id+"F0.wireOp",EDGE,"E6")])],"isStart":false})]}),makeQuery(id+"F1.opExtrude","SWEPT_FACE",FACE,{"disambiguationData":[OSD([subQ0])]})],"blendedInto":[makeQuery(id+"F1.opExtrude","SWEPT_FACE",FACE,{"disambiguationData":[OSD([subQ0])]})]});}
            var Q53;
            {var subQ0=sQuery(id+"F2.wireOp",EDGE,"E7.right");var subQ1=sQuery(id+"F2.wireOp",EDGE,"E7.top");var subQ2=sQuery(id+"F0.wireOp",EDGE,"E2");var subQ3=sQuery(id+"F0.wireOp",EDGE,"E0.bottom");Q53=makeQuery(id+"F7.opFillet","BLEND_EDGE",EDGE,{"blendedFrom":[makeQuery(id+"F6.opFillet","BLEND_EDGE",EDGE,{"blendedFrom":[makeQuery(id+"F3.boolean.opBoolean","COPY",EDGE,{"derivedFrom":makeQuery(id+"F3.opExtrude","SWEPT_EDGE",EDGE,{"disambiguationData":[OSD([subQ3,subQ2,subQ1,subQ0])]})}),makeQuery(id+"F1.opExtrude","CAP_FACE",FACE,{"disambiguationData":[OSD([subQ3,sQuery(id+"F0.wireOp",EDGE,"E0.top"),sQuery(id+"F0.wireOp",EDGE,"E0.right"),sQuery(id+"F0.wireOp",EDGE,"E1"),subQ2,sQuery(id+"F0.wireOp",EDGE,"E5"),sQuery(id+"F0.wireOp",EDGE,"E6")])],"isStart":false})],"blendedInto":[makeQuery(id+"F1.opExtrude","CAP_FACE",FACE,{"disambiguationData":[OSD([subQ3,sQuery(id+"F0.wireOp",EDGE,"E0.top"),sQuery(id+"F0.wireOp",EDGE,"E0.right"),sQuery(id+"F0.wireOp",EDGE,"E1"),subQ2,sQuery(id+"F0.wireOp",EDGE,"E5"),sQuery(id+"F0.wireOp",EDGE,"E6")])],"isStart":false})]}),makeQuery(id+"F6.opFillet","BLEND_FACE",FACE,{"disambiguationData":[OSD([subQ3,subQ2,subQ1,subQ0])]})],"blendedInto":[makeQuery(id+"F6.opFillet","BLEND_FACE",FACE,{"disambiguationData":[OSD([subQ3,subQ2,subQ1,subQ0])]})]});}
            var Q54;
            Q54=makeQuery(id+"F1.opExtrude","CAP_EDGE",EDGE,{"disambiguationData":[OSD([sQuery(id+"F0.wireOp",EDGE,"E5")])],"isStart":true});
            var Q55;
            {var subQ0=sQuery(id+"F2.wireOp",EDGE,"E8.right");var subQ1=sQuery(id+"F2.wireOp",EDGE,"E8.top");var subQ2=sQuery(id+"F0.wireOp",EDGE,"E2");var subQ3=sQuery(id+"F0.wireOp",EDGE,"E0.bottom");Q55=makeQuery(id+"F7.opFillet","BLEND_EDGE",EDGE,{"blendedFrom":[makeQuery(id+"F6.opFillet","BLEND_EDGE",EDGE,{"blendedFrom":[makeQuery(id+"F3.boolean.opBoolean","COPY",EDGE,{"derivedFrom":makeQuery(id+"F3.opExtrude","SWEPT_EDGE",EDGE,{"disambiguationData":[OSD([subQ3,subQ2,subQ1,subQ0])]})}),makeQuery(id+"F1.opExtrude","CAP_FACE",FACE,{"disambiguationData":[OSD([subQ3,sQuery(id+"F0.wireOp",EDGE,"E0.top"),sQuery(id+"F0.wireOp",EDGE,"E0.right"),sQuery(id+"F0.wireOp",EDGE,"E1"),subQ2,sQuery(id+"F0.wireOp",EDGE,"E5"),sQuery(id+"F0.wireOp",EDGE,"E6")])],"isStart":true})],"blendedInto":[makeQuery(id+"F1.opExtrude","CAP_FACE",FACE,{"disambiguationData":[OSD([subQ3,sQuery(id+"F0.wireOp",EDGE,"E0.top"),sQuery(id+"F0.wireOp",EDGE,"E0.right"),sQuery(id+"F0.wireOp",EDGE,"E1"),subQ2,sQuery(id+"F0.wireOp",EDGE,"E5"),sQuery(id+"F0.wireOp",EDGE,"E6")])],"isStart":true})]}),makeQuery(id+"F6.opFillet","BLEND_FACE",FACE,{"disambiguationData":[OSD([subQ3,subQ2,subQ1,subQ0])]})],"blendedInto":[makeQuery(id+"F6.opFillet","BLEND_FACE",FACE,{"disambiguationData":[OSD([subQ3,subQ2,subQ1,subQ0])]})]});}
            var Q56;
            Q56=makeQuery(id+"F5.boolean.opBoolean","INTERSECT",EDGE,{"derivedFrom":[makeQuery(id+"F1.opExtrude","SWEPT_FACE",FACE,{"disambiguationData":[OSD([sQuery(id+"F0.wireOp",EDGE,"E1")])]}),makeQuery(id+"F5.opExtrude","SWEPT_FACE",FACE,{"disambiguationData":[OSD([sQuery(id+"F4.wireOp",EDGE,"E11.top")])]})]});
            var Q57;
            Q57=makeQuery(id+"F5.boolean.opBoolean","INTERSECT",EDGE,{"derivedFrom":[makeQuery(id+"F1.opExtrude","SWEPT_FACE",FACE,{"disambiguationData":[OSD([sQuery(id+"F0.wireOp",EDGE,"E5")])]}),makeQuery(id+"F5.opExtrude","SWEPT_FACE",FACE,{"disambiguationData":[OSD([sQuery(id+"F4.wireOp",EDGE,"E10.top")])]})]});
            var Q58;
            {var subQ0=sQuery(id+"F0.wireOp",EDGE,"E0.bottom");var subQ1=sQuery(id+"F0.wireOp",EDGE,"E2");Q58=makeQuery(id+"F7.opFillet","BLEND_EDGE",EDGE,{"blendedFrom":[makeQuery(id+"F6.opFillet","BLEND_EDGE",EDGE,{"blendedFrom":[makeQuery(id+"F3.boolean.opBoolean","COPY",EDGE,{"derivedFrom":makeQuery(id+"F3.opExtrude","SWEPT_EDGE",EDGE,{"disambiguationData":[OSD([subQ0,subQ1,sQuery(id+"F2.wireOp",EDGE,"E8.top"),sQuery(id+"F2.wireOp",EDGE,"E8.right")])]})}),makeQuery(id+"F1.opExtrude","CAP_FACE",FACE,{"disambiguationData":[OSD([subQ0,sQuery(id+"F0.wireOp",EDGE,"E0.top"),sQuery(id+"F0.wireOp",EDGE,"E0.right"),sQuery(id+"F0.wireOp",EDGE,"E1"),subQ1,sQuery(id+"F0.wireOp",EDGE,"E5"),sQuery(id+"F0.wireOp",EDGE,"E6")])],"isStart":true})],"blendedInto":[makeQuery(id+"F1.opExtrude","CAP_FACE",FACE,{"disambiguationData":[OSD([subQ0,sQuery(id+"F0.wireOp",EDGE,"E0.top"),sQuery(id+"F0.wireOp",EDGE,"E0.right"),sQuery(id+"F0.wireOp",EDGE,"E1"),subQ1,sQuery(id+"F0.wireOp",EDGE,"E5"),sQuery(id+"F0.wireOp",EDGE,"E6")])],"isStart":true})]}),makeQuery(id+"F1.opExtrude","SWEPT_FACE",FACE,{"disambiguationData":[OSD([subQ0])]})],"blendedInto":[makeQuery(id+"F1.opExtrude","SWEPT_FACE",FACE,{"disambiguationData":[OSD([subQ0])]})]});}
            var Q59;
            Q59=makeQuery(id+"F5.boolean.opBoolean","INTERSECT",EDGE,{"derivedFrom":[makeQuery(id+"F1.opExtrude","SWEPT_FACE",FACE,{"disambiguationData":[OSD([sQuery(id+"F0.wireOp",EDGE,"E1")])]}),makeQuery(id+"F5.opExtrude","SWEPT_FACE",FACE,{"disambiguationData":[OSD([sQuery(id+"F4.wireOp",EDGE,"E11.bottom")])]})]});
            var Q60;
            Q60=makeQuery(id+"F5.boolean.opBoolean","INTERSECT",EDGE,{"derivedFrom":[makeQuery(id+"F1.opExtrude","SWEPT_FACE",FACE,{"disambiguationData":[OSD([sQuery(id+"F0.wireOp",EDGE,"E5")])]}),makeQuery(id+"F5.opExtrude","SWEPT_FACE",FACE,{"disambiguationData":[OSD([sQuery(id+"F4.wireOp",EDGE,"E10.bottom")])]})]});
            var Q61;
            Q61=makeQuery(id+"F5.boolean.opBoolean","INTERSECT",EDGE,{"derivedFrom":[makeQuery(id+"F1.opExtrude","SWEPT_FACE",FACE,{"disambiguationData":[OSD([sQuery(id+"F0.wireOp",EDGE,"E2")])]}),makeQuery(id+"F5.opExtrude","SWEPT_FACE",FACE,{"disambiguationData":[OSD([sQuery(id+"F4.wireOp",EDGE,"E10.right")])]})]});
            var Q62;
            Q62=makeQuery(id+"F5.boolean.opBoolean","INTERSECT",EDGE,{"derivedFrom":[makeQuery(id+"F1.opExtrude","SWEPT_FACE",FACE,{"disambiguationData":[OSD([sQuery(id+"F0.wireOp",EDGE,"E5")])]}),makeQuery(id+"F5.opExtrude","SWEPT_FACE",FACE,{"disambiguationData":[OSD([sQuery(id+"F4.wireOp",EDGE,"E9.top")])]})]});
            var Q63;
            {var subQ0=sQuery(id+"F0.wireOp",EDGE,"E5");var subQ1=sQuery(id+"F0.wireOp",EDGE,"E6");Q63=makeQuery(id+"F5.boolean.opBoolean","SPLIT",EDGE,{"disambiguationData":[TD([makeQuery(id+"F5.opExtrude","SWEPT_FACE",FACE,{"disambiguationData":[OSD([sQuery(id+"F4.wireOp",EDGE,"E10.top")])]})])],"derivedFrom":makeQuery(id+"F1.opExtrude","SWEPT_EDGE",EDGE,{"disambiguationData":[OSD([subQ0,subQ1])]})});}
            var Q64;
            {var subQ0=sQuery(id+"F0.wireOp",EDGE,"E5");var subQ1=sQuery(id+"F0.wireOp",EDGE,"E6");Q64=makeQuery(id+"F5.boolean.opBoolean","SPLIT",EDGE,{"disambiguationData":[TD([makeQuery(id+"F5.opExtrude","SWEPT_FACE",FACE,{"disambiguationData":[OSD([sQuery(id+"F4.wireOp",EDGE,"E9.bottom")])]})])],"derivedFrom":makeQuery(id+"F1.opExtrude","SWEPT_EDGE",EDGE,{"disambiguationData":[OSD([subQ0,subQ1])]})});}
            var Q65;
            {var subQ0=sQuery(id+"F0.wireOp",EDGE,"E2");var subQ1=sQuery(id+"F0.wireOp",EDGE,"E6");Q65=makeQuery(id+"F5.boolean.opBoolean","SPLIT",EDGE,{"disambiguationData":[TD([makeQuery(id+"F5.opExtrude","SWEPT_FACE",FACE,{"disambiguationData":[OSD([sQuery(id+"F4.wireOp",EDGE,"E9.bottom")])]})])],"derivedFrom":makeQuery(id+"F1.opExtrude","SWEPT_EDGE",EDGE,{"disambiguationData":[OSD([subQ0,subQ1])]})});}
            var Q66;
            {var subQ0=sQuery(id+"F0.wireOp",EDGE,"E6");var subQ1=sQuery(id+"F0.wireOp",EDGE,"E5");Q66=makeQuery(id+"F5.boolean.opBoolean","SPLIT",EDGE,{"disambiguationData":[TD([makeQuery(id+"F5.opExtrude","SWEPT_FACE",FACE,{"disambiguationData":[OSD([sQuery(id+"F4.wireOp",EDGE,"E10.bottom")])]})])],"derivedFrom":makeQuery(id+"F1.opExtrude","SWEPT_EDGE",EDGE,{"disambiguationData":[OSD([subQ1,subQ0])]})});}
            var Q67;
            {var subQ0=sQuery(id+"F0.wireOp",EDGE,"E6");var subQ1=sQuery(id+"F0.wireOp",EDGE,"E5");Q67=makeQuery(id+"F5.boolean.opBoolean","SPLIT",EDGE,{"disambiguationData":[TD([makeQuery(id+"F5.opExtrude","SWEPT_FACE",FACE,{"disambiguationData":[OSD([sQuery(id+"F4.wireOp",EDGE,"E9.top")])]})])],"derivedFrom":makeQuery(id+"F1.opExtrude","SWEPT_EDGE",EDGE,{"disambiguationData":[OSD([subQ1,subQ0])]})});}
            var Q68;
            {var subQ0=sQuery(id+"F0.wireOp",EDGE,"E2");var subQ1=sQuery(id+"F0.wireOp",EDGE,"E6");Q68=makeQuery(id+"F5.boolean.opBoolean","SPLIT",EDGE,{"disambiguationData":[TD([makeQuery(id+"F5.opExtrude","SWEPT_FACE",FACE,{"disambiguationData":[OSD([sQuery(id+"F4.wireOp",EDGE,"E10.top")])]})])],"derivedFrom":makeQuery(id+"F1.opExtrude","SWEPT_EDGE",EDGE,{"disambiguationData":[OSD([subQ0,subQ1])]})});}
            var Q69;
            {var subQ0=sQuery(id+"F0.wireOp",EDGE,"E6");var subQ1=sQuery(id+"F0.wireOp",EDGE,"E2");Q69=makeQuery(id+"F5.boolean.opBoolean","SPLIT",EDGE,{"disambiguationData":[TD([makeQuery(id+"F5.opExtrude","SWEPT_FACE",FACE,{"disambiguationData":[OSD([sQuery(id+"F4.wireOp",EDGE,"E9.top")])]})])],"derivedFrom":makeQuery(id+"F1.opExtrude","SWEPT_EDGE",EDGE,{"disambiguationData":[OSD([subQ1,subQ0])]})});}
            var Q70;
            {var subQ0=sQuery(id+"F0.wireOp",EDGE,"E6");var subQ1=sQuery(id+"F0.wireOp",EDGE,"E2");Q70=makeQuery(id+"F5.boolean.opBoolean","SPLIT",EDGE,{"disambiguationData":[TD([makeQuery(id+"F5.opExtrude","SWEPT_FACE",FACE,{"disambiguationData":[OSD([sQuery(id+"F4.wireOp",EDGE,"E10.bottom")])]})])],"derivedFrom":makeQuery(id+"F1.opExtrude","SWEPT_EDGE",EDGE,{"disambiguationData":[OSD([subQ1,subQ0])]})});}
            var Q71;
            {var subQ0=sQuery(id+"F0.wireOp",EDGE,"E5");var subQ1=sQuery(id+"F0.wireOp",EDGE,"E1");Q71=makeQuery(id+"F5.boolean.opBoolean","SPLIT",EDGE,{"disambiguationData":[TD([makeQuery(id+"F5.opExtrude","SWEPT_FACE",FACE,{"disambiguationData":[OSD([sQuery(id+"F4.wireOp",EDGE,"E9.top")])]})])],"derivedFrom":makeQuery(id+"F1.opExtrude","SWEPT_EDGE",EDGE,{"disambiguationData":[OSD([subQ1,subQ0])]})});}
            var Q72;
            Q72=makeQuery(id+"F5.boolean.opBoolean","INTERSECT",EDGE,{"derivedFrom":[makeQuery(id+"F1.opExtrude","SWEPT_FACE",FACE,{"disambiguationData":[OSD([sQuery(id+"F0.wireOp",EDGE,"E5")])]}),makeQuery(id+"F5.opExtrude","SWEPT_FACE",FACE,{"disambiguationData":[OSD([sQuery(id+"F4.wireOp",EDGE,"E11.top")])]})]});
            var Q73;
            Q73=makeQuery(id+"F5.boolean.opBoolean","INTERSECT",EDGE,{"derivedFrom":[makeQuery(id+"F1.opExtrude","SWEPT_FACE",FACE,{"disambiguationData":[OSD([sQuery(id+"F0.wireOp",EDGE,"E2")])]}),makeQuery(id+"F5.opExtrude","SWEPT_FACE",FACE,{"disambiguationData":[OSD([sQuery(id+"F4.wireOp",EDGE,"E11.left")])]})]});
            var Q74;
            {var subQ0=sQuery(id+"F0.wireOp",EDGE,"E0.top");var subQ1=sQuery(id+"F0.wireOp",EDGE,"E2");var subQ2=sQuery(id+"F0.wireOp",EDGE,"E0.bottom");Q74=makeQuery(id+"F7.opFillet","BLEND_EDGE",EDGE,{"blendedFrom":[makeQuery(id+"F6.opFillet","BLEND_EDGE",EDGE,{"blendedFrom":[makeQuery(id+"F3.boolean.opBoolean","COPY",EDGE,{"derivedFrom":makeQuery(id+"F3.opExtrude","SWEPT_EDGE",EDGE,{"disambiguationData":[OSD([subQ2,subQ1,sQuery(id+"F2.wireOp",EDGE,"E8.top"),sQuery(id+"F2.wireOp",EDGE,"E8.right")])]})}),makeQuery(id+"F1.opExtrude","CAP_FACE",FACE,{"disambiguationData":[OSD([subQ2,subQ0,sQuery(id+"F0.wireOp",EDGE,"E0.right"),sQuery(id+"F0.wireOp",EDGE,"E1"),subQ1,sQuery(id+"F0.wireOp",EDGE,"E5"),sQuery(id+"F0.wireOp",EDGE,"E6")])],"isStart":true})],"blendedInto":[makeQuery(id+"F1.opExtrude","CAP_FACE",FACE,{"disambiguationData":[OSD([subQ2,subQ0,sQuery(id+"F0.wireOp",EDGE,"E0.right"),sQuery(id+"F0.wireOp",EDGE,"E1"),subQ1,sQuery(id+"F0.wireOp",EDGE,"E5"),sQuery(id+"F0.wireOp",EDGE,"E6")])],"isStart":true})]}),makeQuery(id+"F1.opExtrude","SWEPT_FACE",FACE,{"disambiguationData":[OSD([subQ0])]})],"blendedInto":[makeQuery(id+"F1.opExtrude","SWEPT_FACE",FACE,{"disambiguationData":[OSD([subQ0])]})]});}
            var Q75;
            Q75=makeQuery(id+"F5.boolean.opBoolean","INTERSECT",EDGE,{"derivedFrom":[makeQuery(id+"F1.opExtrude","SWEPT_FACE",FACE,{"disambiguationData":[OSD([sQuery(id+"F0.wireOp",EDGE,"E2")])]}),makeQuery(id+"F5.opExtrude","SWEPT_FACE",FACE,{"disambiguationData":[OSD([sQuery(id+"F4.wireOp",EDGE,"E9.left")])]})]});
            var Q76;
            Q76=makeQuery(id+"F5.boolean.opBoolean","INTERSECT",EDGE,{"derivedFrom":[makeQuery(id+"F1.opExtrude","SWEPT_FACE",FACE,{"disambiguationData":[OSD([sQuery(id+"F0.wireOp",EDGE,"E1")])]}),makeQuery(id+"F5.opExtrude","SWEPT_FACE",FACE,{"disambiguationData":[OSD([sQuery(id+"F4.wireOp",EDGE,"E9.left")])]})]});
            var Q77;
            Q77=makeQuery(id+"F5.boolean.opBoolean","COPY",EDGE,{"derivedFrom":makeQuery(id+"F5.opExtrude","SWEPT_EDGE",EDGE,{"disambiguationData":[OSD([sQuery(id+"F4.wireOp",EDGE,"E11.bottom"),sQuery(id+"F4.wireOp",EDGE,"E11.left")])]})});
            var Q78;
            Q78=makeQuery(id+"F5.boolean.opBoolean","COPY",EDGE,{"derivedFrom":makeQuery(id+"F5.opExtrude","SWEPT_EDGE",EDGE,{"disambiguationData":[OSD([sQuery(id+"F4.wireOp",EDGE,"E10.bottom"),sQuery(id+"F4.wireOp",EDGE,"E10.right")])]})});
            var Q79;
            Q79=makeQuery(id+"F5.boolean.opBoolean","INTERSECT",EDGE,{"derivedFrom":[makeQuery(id+"F1.opExtrude","SWEPT_FACE",FACE,{"disambiguationData":[OSD([sQuery(id+"F0.wireOp",EDGE,"E1")])]}),makeQuery(id+"F5.opExtrude","SWEPT_FACE",FACE,{"disambiguationData":[OSD([sQuery(id+"F4.wireOp",EDGE,"E11.left")])]})]});
            var Q80;
            {var subQ0=sQuery(id+"F0.wireOp",EDGE,"E1");var subQ1=sQuery(id+"F0.wireOp",EDGE,"E5");Q80=makeQuery(id+"F5.boolean.opBoolean","SPLIT",EDGE,{"disambiguationData":[TD([makeQuery(id+"F5.opExtrude","SWEPT_FACE",FACE,{"disambiguationData":[OSD([sQuery(id+"F4.wireOp",EDGE,"E10.top")])]})])],"derivedFrom":makeQuery(id+"F1.opExtrude","SWEPT_EDGE",EDGE,{"disambiguationData":[OSD([subQ0,subQ1])]})});}
            var Q81;
            {var subQ0=sQuery(id+"F0.wireOp",EDGE,"E1");var subQ1=sQuery(id+"F0.wireOp",EDGE,"E5");Q81=makeQuery(id+"F5.boolean.opBoolean","SPLIT",EDGE,{"disambiguationData":[TD([makeQuery(id+"F5.opExtrude","SWEPT_FACE",FACE,{"disambiguationData":[OSD([sQuery(id+"F4.wireOp",EDGE,"E9.bottom")])]})])],"derivedFrom":makeQuery(id+"F1.opExtrude","SWEPT_EDGE",EDGE,{"disambiguationData":[OSD([subQ0,subQ1])]})});}
            var Q82;
            {var subQ0=sQuery(id+"F0.wireOp",EDGE,"E5");var subQ1=sQuery(id+"F0.wireOp",EDGE,"E1");Q82=makeQuery(id+"F5.boolean.opBoolean","SPLIT",EDGE,{"disambiguationData":[TD([makeQuery(id+"F5.opExtrude","SWEPT_FACE",FACE,{"disambiguationData":[OSD([sQuery(id+"F4.wireOp",EDGE,"E10.bottom")])]})])],"derivedFrom":makeQuery(id+"F1.opExtrude","SWEPT_EDGE",EDGE,{"disambiguationData":[OSD([subQ1,subQ0])]})});}
            var Q83;
            Q83=makeQuery(id+"F5.boolean.opBoolean","INTERSECT",EDGE,{"derivedFrom":[makeQuery(id+"F1.opExtrude","SWEPT_FACE",FACE,{"disambiguationData":[OSD([sQuery(id+"F0.wireOp",EDGE,"E1")])]}),makeQuery(id+"F5.opExtrude","SWEPT_FACE",FACE,{"disambiguationData":[OSD([sQuery(id+"F4.wireOp",EDGE,"E10.right")])]})]});
            fillet(context, id + "F8", {"entities" : qUnion([Q0, Q1, Q2, Q3, Q4, Q5, Q6, Q7, Q8, Q9, Q10, Q11, Q12, Q13, Q14, Q15, Q16, Q17, Q18, Q19, Q20, Q21, Q22, Q23, Q24, Q25, Q26, Q27, Q28, Q29, Q30, Q31, Q32, Q33, Q34, Q35, Q36, Q37, Q38, Q39, Q40, Q41, Q42, Q43, Q44, Q45, Q46, Q47, Q48, Q49, Q50, Q51, Q52, Q53, Q54, Q55, Q56, Q57, Q58, Q59, Q60, Q61, Q62, Q63, Q64, Q65, Q66, Q67, Q68, Q69, Q70, Q71, Q72, Q73, Q74, Q75, Q76, Q77, Q78, Q79, Q80, Q81, Q82, Q83]), "radius" : 0.76 * mm, "tangentPropagation" : true, "allowEdgeOverflow" : false});
        }
    });
